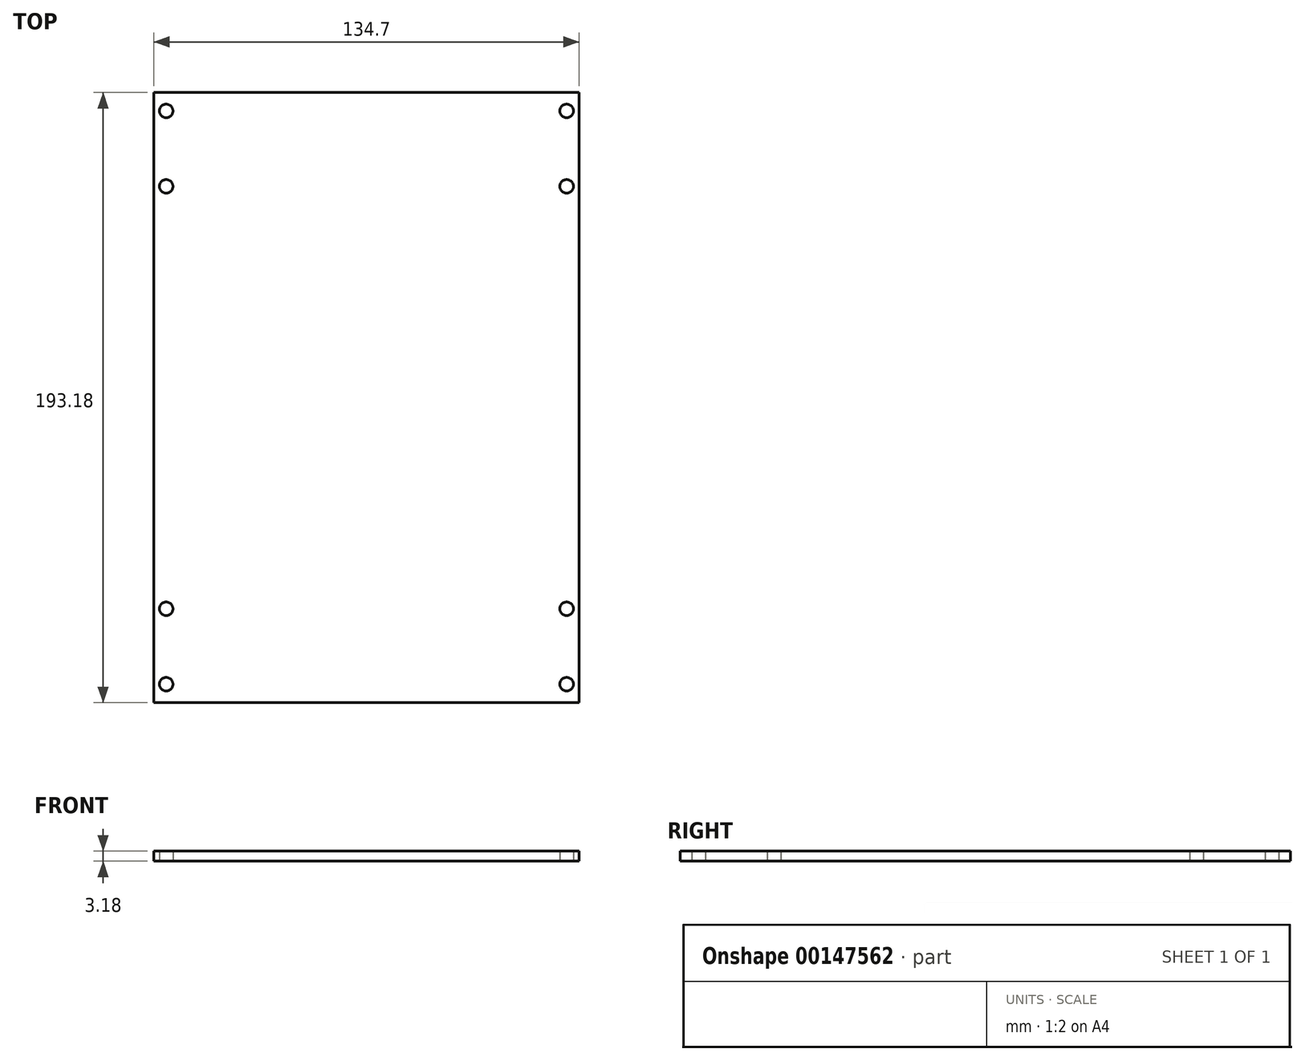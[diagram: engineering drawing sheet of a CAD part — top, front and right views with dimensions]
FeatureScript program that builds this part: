
annotation { "Feature Type Name" : "Feature", "Feature Type Description" : "" }
export const myFeature = defineFeature(function(context is Context, id is Id, definition is map)
    precondition{}
    {
        {
            var Q0;
            Q0=qCreatedBy(makeId("Top.planeOp"),FACE);
            var sketch = newSketch(context, id + "F0", { "sketchPlane" : qUnion([Q0])});
            skPoint(sketch, "E0.rect.middle", {"position": v(0, 0) * mm});
            skLineSegment(sketch, "E1.bottom", {"start": v(67.35, -96.59) * mm, "end": v(-67.35, -96.59) * mm});
            skLineSegment(sketch, "E1.top", {"start": v(67.35, 96.59) * mm, "end": v(-67.35, 96.59) * mm});
            skLineSegment(sketch, "E1.left", {"start": v(67.35, -96.59) * mm, "end": v(67.35, 96.59) * mm});
            skLineSegment(sketch, "E1.right", {"start": v(-67.35, -96.59) * mm, "end": v(-67.35, 96.59) * mm});
            skLineSegment(sketch, "E2.bottom", {"start": v(-63.38, 66.87) * mm, "end": v(63.38, 66.87) * mm, "construction": true});
            skLineSegment(sketch, "E2.top", {"start": v(-63.38, -66.87) * mm, "end": v(63.38, -66.87) * mm, "construction": true});
            skLineSegment(sketch, "E2.left", {"start": v(-63.38, 66.87) * mm, "end": v(-63.38, -66.87) * mm, "construction": true});
            skLineSegment(sketch, "E2.right", {"start": v(63.38, 66.87) * mm, "end": v(63.38, -66.87) * mm, "construction": true});
            skCircle(sketch, "E3", {"center": v(-63.38, 66.87) * mm, "radius": 2.15 * mm});
            skCircle(sketch, "E4", {"center": v(63.38, 66.87) * mm, "radius": 2.15 * mm});
            skCircle(sketch, "E5", {"center": v(-63.38, -66.87) * mm, "radius": 2.15 * mm});
            skCircle(sketch, "E6", {"center": v(63.38, -66.87) * mm, "radius": 2.15 * mm});
            skLineSegment(sketch, "E7", {"start": v(-63.38, 66.87) * mm, "end": v(-63.38, 90.75) * mm, "construction": true});
            skLineSegment(sketch, "E8", {"start": v(63.38, 66.87) * mm, "end": v(63.38, 90.75) * mm, "construction": true});
            skLineSegment(sketch, "E9", {"start": v(63.38, -66.87) * mm, "end": v(63.38, -90.75) * mm, "construction": true});
            skLineSegment(sketch, "E10", {"start": v(-63.38, -66.87) * mm, "end": v(-63.38, -90.75) * mm, "construction": true});
            skLineSegment(sketch, "E11", {"start": v(-63.38, -90.75) * mm, "end": v(-67.35, -90.75) * mm, "construction": true});
            skLineSegment(sketch, "E12", {"start": v(-63.38, -90.75) * mm, "end": v(-63.38, -96.59) * mm, "construction": true});
            skCircle(sketch, "E13", {"center": v(-63.38, -90.75) * mm, "radius": 2.15 * mm});
            skCircle(sketch, "E14", {"center": v(63.38, -90.75) * mm, "radius": 2.15 * mm});
            skCircle(sketch, "E15", {"center": v(63.38, 90.75) * mm, "radius": 2.15 * mm});
            skCircle(sketch, "E16", {"center": v(-63.38, 90.75) * mm, "radius": 2.15 * mm});
            skLineSegment(sketch, "E17", {"start": v(63.38, 90.75) * mm, "end": v(67.35, 90.75) * mm, "construction": true});
            skLineSegment(sketch, "E18", {"start": v(63.38, 90.75) * mm, "end": v(63.38, 96.59) * mm, "construction": true});
            skSolve(sketch);
        }
        {
            var Q0;
            Q0=qSketchRegion(id+"F0",true);
            extrude(context, id + "F1", {"entities" : qUnion([Q0]), "depth" : 3.17 * mm});
        }
    });
